# Revit family: 210_d964a00033364c478ba37ba48b3cb8
name_source: partatom
category: Mechanical Equipment
revit_build: Autodesk Revit 2018 (Build: 20170223_1515(x64)
units: mm (PartAtom-declared; Revit-internal decimal feet)

## family parameters
Always vertical = Yes
Classification = None
Cut with Voids When Loaded = No
Part Type = Breaks Into
Room Calculation Point = No
Round Connector Dimension = Use Diameter
Shared = No
Work Plane-Based = No

## types (1)
- 04010
    DI = 51 mm
    DO = 51 mm
    DZ1 = 222 mm  [stored 0.728346 ft]
    DZ2 = 73 mm  [stored 0.239501 ft]
    Description = Central Vacuum Cleaner CVR 1000
    H = 427 mm  [stored 1.40092 ft]
    H2 = 214 mm
    L2 = 180 mm  [stored 0.590551 ft]
    LB = 126 mm  [stored 0.413386 ft]
    LB1 = 151 mm
    LB2 = 162 mm  [stored 0.531496 ft]
    LB3 = 173 mm
    LT = 90 mm  [stored 0.295276 ft]
    MC Product Code = 04010
    Manufacturer = Flexit
    QmdConnectorList = 201;DI;202;DO
    RI = 26 mm
    RO = 26 mm
    URL = www.flexit.no
    W = 397 mm  [stored 1.30249 ft]
    W1 = 217 mm  [stored 0.711942 ft]
    W22 = 217 mm  [stored 0.711942 ft]
    Z1 = 120 mm
    Z2 = 68 mm
    Z22 = 34 mm
    Z23 = 29 mm
    magiPartTypeId = 210
    magiProductFamilyId = d964a00033364c478ba37ba48b3cb8
    magiProductId = c64b0961a4b04aed9de79bf78cf578

note: [stored X ft] marks values corroborated as IEEE doubles in the binary element streams (Revit-internal decimal feet)

## geometry (parser evidence)
native form markers: Sweep x2
no freeform markers — native parametric forms only
